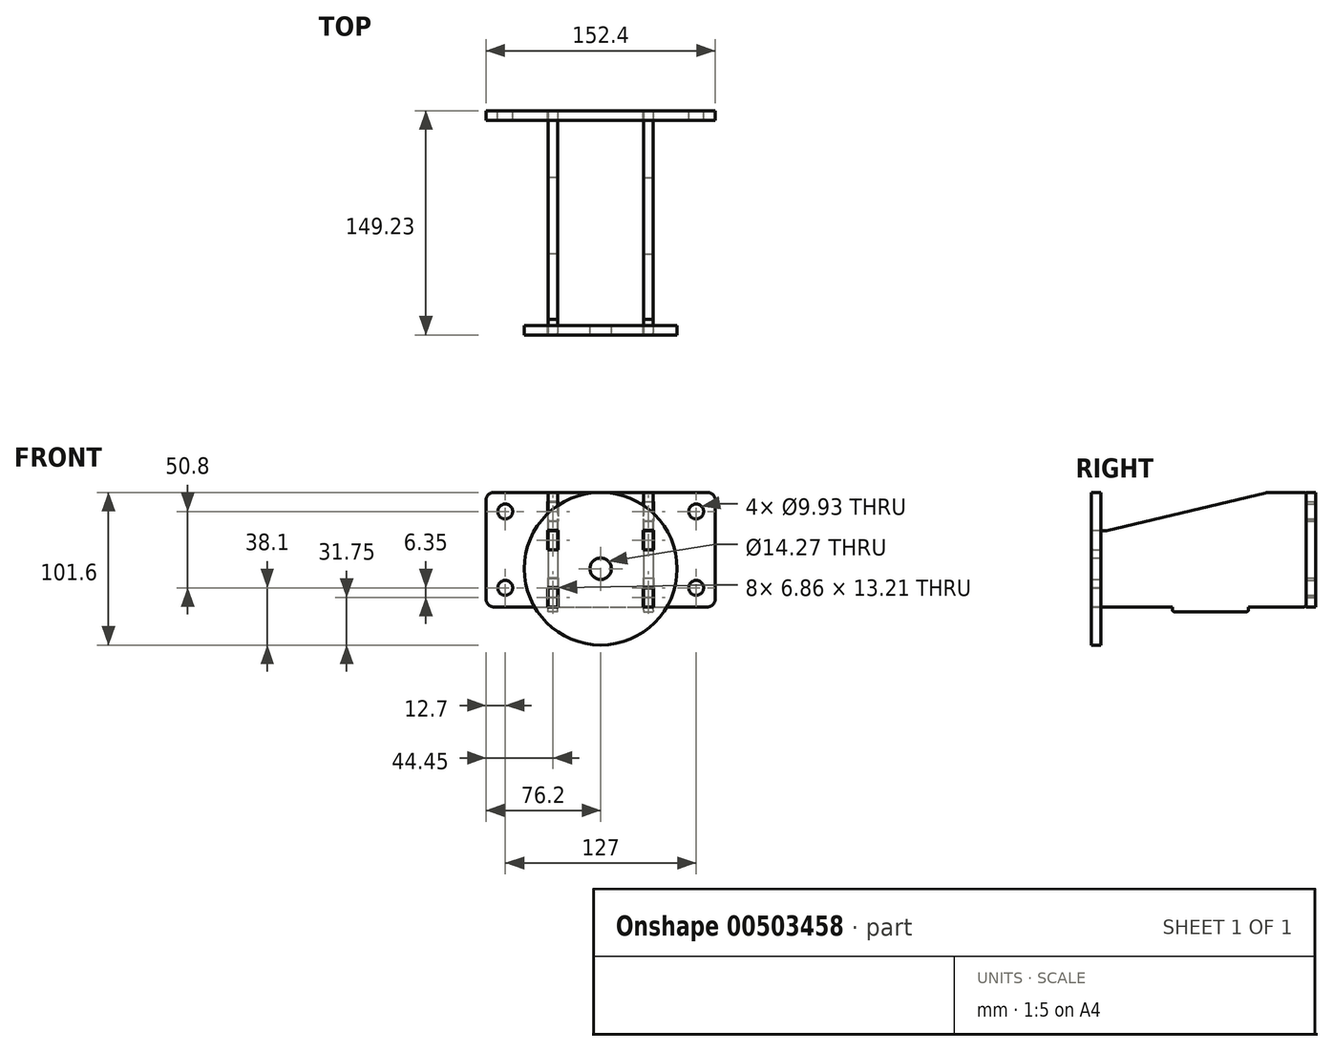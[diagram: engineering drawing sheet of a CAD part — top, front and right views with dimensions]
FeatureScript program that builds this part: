
annotation { "Feature Type Name" : "Feature", "Feature Type Description" : "" }
export const myFeature = defineFeature(function(context is Context, id is Id, definition is map)
    precondition{}
    {
        {
            var Q0;
            Q0=qCreatedBy(makeId("Front.planeOp"),FACE);
            var sketch = newSketch(context, id + "F0", { "sketchPlane" : qUnion([Q0])});
            skCircle(sketch, "E0", {"center": v(0, 0) * mm, "radius": 50.8 * mm});
            skCircle(sketch, "E1", {"center": v(0, 0) * mm, "radius": 7.14 * mm});
            skLineSegment(sketch, "E2.bottom", {"start": v(-28.58, 25.4) * mm, "end": v(-34.93, 25.4) * mm});
            skLineSegment(sketch, "E2.top", {"start": v(-28.57, -25.4) * mm, "end": v(-34.92, -25.4) * mm});
            skLineSegment(sketch, "E2.left", {"start": v(-28.58, 25.4) * mm, "end": v(-28.57, -25.4) * mm});
            skLineSegment(sketch, "E2.right", {"start": v(-34.93, 25.4) * mm, "end": v(-34.93, -25.4) * mm});
            skPoint(sketch, "E2.middle", {"position": v(-31.75, 0) * mm});
            skLineSegment(sketch, "E3.bottom", {"start": v(-35.18, 25.65) * mm, "end": v(-28.32, 25.65) * mm});
            skLineSegment(sketch, "E3.top", {"start": v(-35.18, 12.45) * mm, "end": v(-28.32, 12.45) * mm});
            skLineSegment(sketch, "E3.left", {"start": v(-35.18, 25.65) * mm, "end": v(-35.18, 12.45) * mm});
            skLineSegment(sketch, "E3.right", {"start": v(-28.32, 25.65) * mm, "end": v(-28.32, 12.45) * mm});
            skLineSegment(sketch, "E4.MirrorCS", {"start": v(-28.32, -25.65) * mm, "end": v(-28.32, -12.45) * mm});
            skLineSegment(sketch, "E5.MirrorCS", {"start": v(-35.18, -25.65) * mm, "end": v(-35.18, -12.45) * mm});
            skLineSegment(sketch, "E6.MirrorCS", {"start": v(-35.18, -25.65) * mm, "end": v(-28.32, -25.65) * mm});
            skLineSegment(sketch, "E7.MirrorCS", {"start": v(-35.18, -12.45) * mm, "end": v(-28.32, -12.45) * mm});
            skLineSegment(sketch, "E8.MirrorCS", {"start": v(28.58, 25.4) * mm, "end": v(28.57, -25.4) * mm});
            skLineSegment(sketch, "E9.MirrorCS", {"start": v(35.18, -25.65) * mm, "end": v(28.32, -25.65) * mm});
            skLineSegment(sketch, "E10.MirrorCS", {"start": v(35.18, -25.65) * mm, "end": v(35.18, -12.45) * mm});
            skLineSegment(sketch, "E11.MirrorCS", {"start": v(35.18, 12.45) * mm, "end": v(28.32, 12.45) * mm});
            skLineSegment(sketch, "E12.MirrorCS", {"start": v(28.58, 25.4) * mm, "end": v(34.93, 25.4) * mm});
            skLineSegment(sketch, "E13.MirrorCS", {"start": v(35.18, 25.65) * mm, "end": v(28.32, 25.65) * mm});
            skLineSegment(sketch, "E14.MirrorCS", {"start": v(35.18, 25.65) * mm, "end": v(35.18, 12.45) * mm});
            skLineSegment(sketch, "E15.MirrorCS", {"start": v(35.18, -12.45) * mm, "end": v(28.32, -12.45) * mm});
            skLineSegment(sketch, "E16.MirrorCS", {"start": v(28.32, 25.65) * mm, "end": v(28.32, 12.45) * mm});
            skLineSegment(sketch, "E17.MirrorCS", {"start": v(28.32, -25.65) * mm, "end": v(28.32, -12.45) * mm});
            skLineSegment(sketch, "E18.MirrorCS", {"start": v(28.57, -25.4) * mm, "end": v(34.92, -25.4) * mm});
            skPoint(sketch, "E19.MirrorP", {"position": v(31.75, 0) * mm});
            skLineSegment(sketch, "E20.MirrorCS", {"start": v(34.93, 25.4) * mm, "end": v(34.93, -25.4) * mm});
            skLineSegment(sketch, "E21", {"start": v(28.57, 12.7) * mm, "end": v(34.93, 12.7) * mm});
            skLineSegment(sketch, "E22", {"start": v(28.57, -12.7) * mm, "end": v(34.93, -12.7) * mm});
            skLineSegment(sketch, "E23", {"start": v(-34.92, -12.7) * mm, "end": v(-28.57, -12.7) * mm});
            skLineSegment(sketch, "E24", {"start": v(-34.93, 12.7) * mm, "end": v(-28.57, 12.7) * mm});
            skSolve(sketch);
        }
        {
            var Q0;
            Q0=makeQuery(id+"F0.imprint","IMPRINT",FACE,{"disambiguationData":[TD([[makeQuery(id+"F0.imprint","IMPRINT",EDGE,{"derivedFrom":sQuery(id+"F0.wireOp",EDGE,"E0")}),1.0]])]});
            var Q1;
            {var subQ0=sQuery(id+"F0.wireOp",EDGE,"E3.top");var subQ1=sQuery(id+"F0.wireOp",EDGE,"E2.left");var subQ2=makeQuery(id+"F0.imprint","INTERSECT",VERTEX,{"derivedFrom":[subQ1,subQ0]});Q1=makeQuery(id+"F0.imprint","IMPRINT",FACE,{"disambiguationData":[TD([[makeQuery(id+"F0.imprint","IMPRINT",EDGE,{"disambiguationData":[TD([[subQ2,-1.0]])],"derivedFrom":subQ1}),-1.0]])]});}
            var Q2;
            {var subQ0=sQuery(id+"F0.wireOp",EDGE,"E11.MirrorCS");var subQ1=sQuery(id+"F0.wireOp",EDGE,"E8.MirrorCS");var subQ2=makeQuery(id+"F0.imprint","INTERSECT",VERTEX,{"derivedFrom":[subQ1,subQ0]});Q2=makeQuery(id+"F0.imprint","IMPRINT",FACE,{"disambiguationData":[TD([[makeQuery(id+"F0.imprint","IMPRINT",EDGE,{"disambiguationData":[TD([[subQ2,-1.0]])],"derivedFrom":subQ1}),1.0]])]});}
            extrude(context, id + "F1", {"entities" : qUnion([Q0, Q1, Q2]), "depth" : 6.35 * mm, "offsetDistance" : 25.4 * mm});
        }
        {
            var Q0;
            {var subQ0=sQuery(id+"F0.wireOp",EDGE,"E12.MirrorCS");Q0=makeQuery(id+"F0.imprint","IMPRINT",FACE,{"disambiguationData":[TD([[makeQuery(id+"F0.imprint","IMPRINT",EDGE,{"derivedFrom":subQ0}),-1.0]])]});}
            var Q1;
            {var subQ0=sQuery(id+"F0.wireOp",EDGE,"E11.MirrorCS");var subQ1=sQuery(id+"F0.wireOp",EDGE,"E8.MirrorCS");var subQ2=makeQuery(id+"F0.imprint","INTERSECT",VERTEX,{"derivedFrom":[subQ1,subQ0]});Q1=makeQuery(id+"F0.imprint","IMPRINT",FACE,{"disambiguationData":[TD([[makeQuery(id+"F0.imprint","IMPRINT",EDGE,{"disambiguationData":[TD([[subQ2,-1.0]])],"derivedFrom":subQ1}),1.0]])]});}
            var Q2;
            {var subQ0=sQuery(id+"F0.wireOp",EDGE,"E18.MirrorCS");Q2=makeQuery(id+"F0.imprint","IMPRINT",FACE,{"disambiguationData":[TD([[makeQuery(id+"F0.imprint","IMPRINT",EDGE,{"derivedFrom":subQ0}),1.0]])]});}
            var Q3;
            {var subQ0=sQuery(id+"F0.wireOp",EDGE,"E21");Q3=makeQuery(id+"F0.imprint","IMPRINT",FACE,{"disambiguationData":[TD([[makeQuery(id+"F0.imprint","IMPRINT",EDGE,{"derivedFrom":subQ0}),-1.0]])]});}
            var Q4;
            {var subQ0=sQuery(id+"F0.wireOp",EDGE,"E22");Q4=makeQuery(id+"F0.imprint","IMPRINT",FACE,{"disambiguationData":[TD([[makeQuery(id+"F0.imprint","IMPRINT",EDGE,{"derivedFrom":subQ0}),1.0]])]});}
            var Q5;
            Q5=sQuery(id+"F0.wireOp",EDGE,"E2.right");
            var Q6;
            Q6=sQuery(id+"F0.wireOp",EDGE,"E2.bottom");
            var Q7;
            Q7=sQuery(id+"F0.wireOp",EDGE,"E2.left");
            var Q8;
            Q8=sQuery(id+"F0.wireOp",EDGE,"E2.top");
            var Q9;
            Q9=sQuery(id+"F0.wireOp",EDGE,"E12.MirrorCS");
            var Q10;
            Q10=sQuery(id+"F0.wireOp",EDGE,"E8.MirrorCS");
            var Q11;
            Q11=sQuery(id+"F0.wireOp",EDGE,"E20.MirrorCS");
            var Q12;
            Q12=sQuery(id+"F0.wireOp",EDGE,"E18.MirrorCS");
            extrude(context, id + "F2", {"entities" : qUnion([Q0, Q1, Q2, Q3, Q4]), "surfaceEntities" : qUnion([Q5, Q6, Q7, Q8, Q9, Q10, Q11, Q12]), "oppositeDirection" : true, "depth" : 136.53 * mm, "offsetDistance" : 25.4 * mm});
        }
        {
            var Q0;
            {var subQ0=sQuery(id+"F0.wireOp",EDGE,"E12.MirrorCS");Q0=makeQuery(id+"F0.imprint","IMPRINT",FACE,{"disambiguationData":[TD([[makeQuery(id+"F0.imprint","IMPRINT",EDGE,{"derivedFrom":subQ0}),-1.0]])]});}
            var Q1;
            {var subQ0=sQuery(id+"F0.wireOp",EDGE,"E18.MirrorCS");Q1=makeQuery(id+"F0.imprint","IMPRINT",FACE,{"disambiguationData":[TD([[makeQuery(id+"F0.imprint","IMPRINT",EDGE,{"derivedFrom":subQ0}),1.0]])]});}
            var Q2;
            Q2=sQuery(id+"F0.wireOp",EDGE,"E21");
            extrude(context, id + "F3", {"entities" : qUnion([Q0, Q1]), "operationType" : NewBodyOperationType.ADD, "surfaceOperationType" : NewSurfaceOperationType.ADD, "surfaceEntities" : qUnion([Q2]), "depth" : 6.1 * mm, "offsetDistance" : 25.4 * mm});
        }
        {
            var Q0;
            {var subQ0=sQuery(id+"F0.wireOp",EDGE,"E20.MirrorCS");Q0=makeQuery(id+"F3.boolean.opBoolean","MERGE",FACE,{"derivedFrom":[makeQuery(id+"F2.opExtrude","SWEPT_FACE",FACE,{"disambiguationData":[OSD([subQ0])]}),makeQuery(id+"F3.opExtrude","SWEPT_FACE",FACE,{"disambiguationData":[OSD([subQ0]),TDD([makeQuery(id+"F0.imprint","IMPRINT",EDGE,{"disambiguationData":[TD([[makeQuery(id+"F0.imprint","INTERSECT",VERTEX,{"derivedFrom":[sQuery(id+"F0.wireOp",EDGE,"E12.MirrorCS"),subQ0]}),-1.0]])],"derivedFrom":subQ0})])]}),makeQuery(id+"F3.opExtrude","SWEPT_FACE",FACE,{"disambiguationData":[OSD([subQ0]),TDD([makeQuery(id+"F0.imprint","IMPRINT",EDGE,{"disambiguationData":[TD([[makeQuery(id+"F0.imprint","INTERSECT",VERTEX,{"derivedFrom":[sQuery(id+"F0.wireOp",EDGE,"E18.MirrorCS"),subQ0]}),1.0]])],"derivedFrom":subQ0})])]})]});}
            var sketch = newSketch(context, id + "F4", { "sketchPlane" : qUnion([Q0])});
            skLineSegment(sketch, "E25", {"start": v(136.52, -25.4) * mm, "end": v(136.52, 50.8) * mm});
            skLineSegment(sketch, "E26", {"start": v(136.52, 50.8) * mm, "end": v(111.12, 50.8) * mm});
            skLineSegment(sketch, "E27", {"start": v(136.53, -25.4) * mm, "end": v(3.9, -25.4) * mm});
            skLineSegment(sketch, "E28", {"start": v(3.9, -25.4) * mm, "end": v(3.9, 25.4) * mm});
            skLineSegment(sketch, "E29", {"start": v(3.9, 25.4) * mm, "end": v(111.13, 50.8) * mm});
            skSolve(sketch);
        }
        {
            var Q0;
            {var subQ5=sQuery(id+"F4.wireOp",EDGE,"E26");Q0=makeQuery(id+"F4.imprint","IMPRINT",FACE,{"disambiguationData":[TD([[makeQuery(id+"F4.imprint","IMPRINT",EDGE,{"derivedFrom":subQ5}),1.0]])]});}
            extrude(context, id + "F5", {"entities" : qUnion([Q0]), "operationType" : NewBodyOperationType.ADD, "oppositeDirection" : true, "depth" : 6.35 * mm, "offsetDistance" : 25.4 * mm});
        }
        {
            var Q0;
            Q0=makeQuery(id+"F5.boolean.opBoolean","MERGE",FACE,{"derivedFrom":[makeQuery(id+"F2.opExtrude","CAP_FACE",FACE,{"disambiguationData":[OSD([sQuery(id+"F0.wireOp",EDGE,"E8.MirrorCS"),sQuery(id+"F0.wireOp",EDGE,"E12.MirrorCS"),sQuery(id+"F0.wireOp",EDGE,"E18.MirrorCS"),sQuery(id+"F0.wireOp",EDGE,"E20.MirrorCS")])],"isStart":false}),makeQuery(id+"F5.opExtrude","SWEPT_FACE",FACE,{"disambiguationData":[OSD([sQuery(id+"F4.wireOp",EDGE,"E25")])]})]});
            var sketch = newSketch(context, id + "F6", { "sketchPlane" : qUnion([Q0])});
            skLineSegment(sketch, "E30", {"start": v(-34.93, 44.45) * mm, "end": v(-28.58, 44.45) * mm});
            skLineSegment(sketch, "E31", {"start": v(-34.93, 31.75) * mm, "end": v(-28.58, 31.75) * mm});
            skLineSegment(sketch, "E32", {"start": v(-34.93, -19.05) * mm, "end": v(-28.58, -19.05) * mm});
            skLineSegment(sketch, "E33", {"start": v(-34.93, -6.35) * mm, "end": v(-28.58, -6.35) * mm});
            skSolve(sketch);
        }
        {
            var Q0;
            {var subQ0=sQuery(id+"F6.wireOp",EDGE,"E30");Q0=makeQuery(id+"F6.imprint","IMPRINT",FACE,{"disambiguationData":[TD([[makeQuery(id+"F6.imprint","IMPRINT",EDGE,{"derivedFrom":subQ0}),-1.0]])]});}
            var Q1;
            {var subQ0=sQuery(id+"F6.wireOp",EDGE,"E32");Q1=makeQuery(id+"F6.imprint","IMPRINT",FACE,{"disambiguationData":[TD([[makeQuery(id+"F6.imprint","IMPRINT",EDGE,{"derivedFrom":subQ0}),1.0]])]});}
            extrude(context, id + "F7", {"entities" : qUnion([Q0, Q1]), "operationType" : NewBodyOperationType.ADD, "depth" : 6.1 * mm, "offsetDistance" : 25.4 * mm});
        }
        {
            var Q0;
            Q0=makeQuery(id+"F3.opExtrude","CAP_EDGE",EDGE,{"disambiguationData":[OSD([sQuery(id+"F0.wireOp",EDGE,"E12.MirrorCS")])],"isStart":false});
            var Q1;
            Q1=makeQuery(id+"F3.opExtrude","CAP_EDGE",EDGE,{"disambiguationData":[OSD([sQuery(id+"F0.wireOp",EDGE,"E21")])],"isStart":false});
            var Q2;
            Q2=makeQuery(id+"F3.opExtrude","CAP_EDGE",EDGE,{"disambiguationData":[OSD([sQuery(id+"F0.wireOp",EDGE,"E22")])],"isStart":false});
            var Q3;
            Q3=makeQuery(id+"F3.opExtrude","CAP_EDGE",EDGE,{"disambiguationData":[OSD([sQuery(id+"F0.wireOp",EDGE,"E18.MirrorCS")])],"isStart":false});
            var Q4;
            Q4=makeQuery(id+"F7.opExtrude","CAP_EDGE",EDGE,{"disambiguationData":[OSD([sQuery(id+"F6.wireOp",EDGE,"E32")])],"isStart":false});
            var Q5;
            Q5=makeQuery(id+"F7.opExtrude","CAP_EDGE",EDGE,{"disambiguationData":[OSD([sQuery(id+"F6.wireOp",EDGE,"E33")])],"isStart":false});
            var Q6;
            Q6=makeQuery(id+"F7.opExtrude","CAP_EDGE",EDGE,{"disambiguationData":[OSD([sQuery(id+"F6.wireOp",EDGE,"E31")])],"isStart":false});
            var Q7;
            Q7=makeQuery(id+"F7.opExtrude","CAP_EDGE",EDGE,{"disambiguationData":[OSD([sQuery(id+"F6.wireOp",EDGE,"E30")])],"isStart":false});
            var Q8;
            Q8=makeQuery(id+"F2.opExtrude","CAP_EDGE",EDGE,{"disambiguationData":[OSD([sQuery(id+"F0.wireOp",EDGE,"E18.MirrorCS")])],"isStart":false});
            var Q9;
            Q9=makeQuery(id+"F5.opExtrude","SWEPT_EDGE",EDGE,{"disambiguationData":[OSD([sQuery(id+"F4.wireOp",EDGE,"E25"),sQuery(id+"F4.wireOp",EDGE,"E26")])]});
            fillet(context, id + "F8", {"entities" : qUnion([Q0, Q1, Q2, Q3, Q4, Q5, Q6, Q7, Q8, Q9]), "radius" : 1.27 * mm, "tangentPropagation" : true, "allowEdgeOverflow" : false});
        }
        {
            var Q0;
            Q0=makeQuery(id+"F5.opExtrude","SWEPT_EDGE",EDGE,{"disambiguationData":[OSD([sQuery(id+"F0.wireOp",EDGE,"E12.MirrorCS"),sQuery(id+"F0.wireOp",EDGE,"E20.MirrorCS"),sQuery(id+"F4.wireOp",EDGE,"E28"),sQuery(id+"F4.wireOp",EDGE,"E29")])]});
            var Q1;
            Q1=makeQuery(id+"F5.opExtrude","SWEPT_EDGE",EDGE,{"disambiguationData":[OSD([sQuery(id+"F4.wireOp",EDGE,"E26"),sQuery(id+"F4.wireOp",EDGE,"E29")])]});
            fillet(context, id + "F9", {"entities" : qUnion([Q0, Q1]), "radius" : 12.7 * mm, "allowEdgeOverflow" : false});
        }
        {
            var Q0;
            Q0=makeQuery(id+"F7.opExtrude","CAP_FACE",FACE,{"disambiguationData":[OSD([sQuery(id+"F0.wireOp",EDGE,"E8.MirrorCS"),sQuery(id+"F0.wireOp",EDGE,"E20.MirrorCS"),sQuery(id+"F4.wireOp",EDGE,"E25"),sQuery(id+"F6.wireOp",EDGE,"E30"),sQuery(id+"F6.wireOp",EDGE,"E31")])],"isStart":false});
            var sketch = newSketch(context, id + "F10", { "sketchPlane" : qUnion([Q0])});
            skLineSegment(sketch, "E34", {"start": v(-95.05, -25.4) * mm, "end": v(104.43, -25.4) * mm, "construction": true});
            skLineSegment(sketch, "E35", {"start": v(-97.99, 50.8) * mm, "end": v(99.94, 50.8) * mm, "construction": true});
            skLineSegment(sketch, "E36", {"start": v(-76.2, 66.04) * mm, "end": v(-76.2, -54.32) * mm, "construction": true});
            skLineSegment(sketch, "E37", {"start": v(99.84, 72.1) * mm, "end": v(99.84, -54.32) * mm, "construction": true});
            skLineSegment(sketch, "E38.bottom", {"start": v(-76.2, 50.8) * mm, "end": v(0, 50.8) * mm});
            skLineSegment(sketch, "E38.top", {"start": v(-76.2, -25.4) * mm, "end": v(0, -25.4) * mm});
            skLineSegment(sketch, "E38.left", {"start": v(-76.2, 50.8) * mm, "end": v(-76.2, -25.4) * mm});
            skLineSegment(sketch, "E38.right", {"start": v(0, 50.8) * mm, "end": v(0, -25.4) * mm});
            skLineSegment(sketch, "E39.MirrorCS", {"start": v(76.2, -25.4) * mm, "end": v(0, -25.4) * mm});
            skLineSegment(sketch, "E40.MirrorCS", {"start": v(76.2, 50.8) * mm, "end": v(0, 50.8) * mm});
            skLineSegment(sketch, "E41.MirrorCS", {"start": v(76.2, 50.8) * mm, "end": v(76.2, -25.4) * mm});
            skCircle(sketch, "E42", {"center": v(-63.5, 38.1) * mm, "radius": 4.97 * mm});
            skCircle(sketch, "E43", {"center": v(-63.5, -12.7) * mm, "radius": 4.97 * mm});
            skCircle(sketch, "E44.MirrorC", {"center": v(63.5, 38.1) * mm, "radius": 4.97 * mm});
            skCircle(sketch, "E45.MirrorC", {"center": v(63.5, -12.7) * mm, "radius": 4.97 * mm});
            skLineSegment(sketch, "E46.bottom", {"start": v(-28.32, 44.7) * mm, "end": v(-35.18, 44.7) * mm});
            skLineSegment(sketch, "E46.top", {"start": v(-28.32, 31.5) * mm, "end": v(-35.18, 31.5) * mm});
            skLineSegment(sketch, "E46.left", {"start": v(-28.32, 44.7) * mm, "end": v(-28.32, 31.5) * mm});
            skLineSegment(sketch, "E46.right", {"start": v(-35.18, 44.7) * mm, "end": v(-35.18, 31.5) * mm});
            skLineSegment(sketch, "E47.0", {"start": v(-34.93, -6.35) * mm, "end": v(-34.93, -19.05) * mm});
            skLineSegment(sketch, "E48.0", {"start": v(-34.93, -6.35) * mm, "end": v(-28.58, -6.35) * mm});
            skLineSegment(sketch, "E49.0", {"start": v(-34.93, -19.05) * mm, "end": v(-28.58, -19.05) * mm});
            skLineSegment(sketch, "E50.0", {"start": v(-28.58, -6.35) * mm, "end": v(-28.58, -19.05) * mm});
            skLineSegment(sketch, "E51.bottom", {"start": v(-28.32, -6.1) * mm, "end": v(-35.18, -6.1) * mm});
            skLineSegment(sketch, "E51.top", {"start": v(-28.32, -19.3) * mm, "end": v(-35.18, -19.3) * mm});
            skLineSegment(sketch, "E51.left", {"start": v(-28.32, -6.1) * mm, "end": v(-28.32, -19.3) * mm});
            skLineSegment(sketch, "E51.right", {"start": v(-35.18, -6.1) * mm, "end": v(-35.18, -19.3) * mm});
            skLineSegment(sketch, "E52.MirrorCS", {"start": v(28.32, -6.1) * mm, "end": v(35.18, -6.1) * mm});
            skLineSegment(sketch, "E53.MirrorCS", {"start": v(34.93, -6.35) * mm, "end": v(28.58, -6.35) * mm});
            skLineSegment(sketch, "E54.MirrorCS", {"start": v(28.32, -19.3) * mm, "end": v(35.18, -19.3) * mm});
            skLineSegment(sketch, "E55.MirrorCS", {"start": v(28.32, 44.7) * mm, "end": v(35.18, 44.7) * mm});
            skLineSegment(sketch, "E56.MirrorCS", {"start": v(28.32, 31.5) * mm, "end": v(35.18, 31.5) * mm});
            skLineSegment(sketch, "E57.MirrorCS", {"start": v(34.93, -19.05) * mm, "end": v(28.58, -19.05) * mm});
            skLineSegment(sketch, "E58.MirrorCS", {"start": v(35.18, -6.1) * mm, "end": v(35.18, -19.3) * mm});
            skLineSegment(sketch, "E59.MirrorCS", {"start": v(28.58, -6.35) * mm, "end": v(28.58, -19.05) * mm});
            skLineSegment(sketch, "E60.MirrorCS", {"start": v(28.32, 44.7) * mm, "end": v(28.32, 31.5) * mm});
            skLineSegment(sketch, "E61.MirrorCS", {"start": v(35.18, 44.7) * mm, "end": v(35.18, 31.5) * mm});
            skLineSegment(sketch, "E62.MirrorCS", {"start": v(28.32, -6.1) * mm, "end": v(28.32, -19.3) * mm});
            skLineSegment(sketch, "E63.MirrorCS", {"start": v(34.93, -6.35) * mm, "end": v(34.93, -19.05) * mm});
            skSolve(sketch);
        }
        {
            var Q0;
            Q0=makeQuery(id+"F10.imprint","IMPRINT",FACE,{"disambiguationData":[TD([[makeQuery(id+"F10.imprint","IMPRINT",EDGE,{"derivedFrom":sQuery(id+"F10.wireOp",EDGE,"kh7ab5N3-OJCW-Qjtw-u9Ue-FteD8OsjeyxH.bottom")}),1.0]])]});
            var Q1;
            Q1=makeQuery(id+"F10.imprint","IMPRINT",FACE,{"disambiguationData":[TD([[makeQuery(id+"F10.imprint","IMPRINT",EDGE,{"derivedFrom":sQuery(id+"F10.wireOp",EDGE,"E38.right")}),1.0]])]});
            var Q2;
            Q2=makeQuery(id+"F10.imprint","IMPRINT",FACE,{"disambiguationData":[TD([[makeQuery(id+"F10.imprint","IMPRINT",EDGE,{"derivedFrom":sQuery(id+"F10.wireOp",EDGE,"E38.bottom")}),-1.0]])]});
            extrude(context, id + "F11", {"entities" : qUnion([Q0, Q1, Q2]), "oppositeDirection" : true, "depth" : 6.35 * mm, "offsetDistance" : 25.4 * mm});
        }
        {
            var Q0;
            Q0=makeQuery(id+"F11.opExtrude","SWEPT_EDGE",EDGE,{"disambiguationData":[OSD([sQuery(id+"F10.wireOp",EDGE,"E38.bottom"),sQuery(id+"F10.wireOp",EDGE,"E38.left")])]});
            var Q1;
            Q1=makeQuery(id+"F11.opExtrude","SWEPT_EDGE",EDGE,{"disambiguationData":[OSD([sQuery(id+"F10.wireOp",EDGE,"E38.top"),sQuery(id+"F10.wireOp",EDGE,"E38.left")])]});
            var Q2;
            Q2=makeQuery(id+"F11.opExtrude","SWEPT_EDGE",EDGE,{"disambiguationData":[OSD([sQuery(id+"F10.wireOp",EDGE,"E39.MirrorCS"),sQuery(id+"F10.wireOp",EDGE,"E41.MirrorCS")])]});
            var Q3;
            Q3=makeQuery(id+"F11.opExtrude","SWEPT_EDGE",EDGE,{"disambiguationData":[OSD([sQuery(id+"F10.wireOp",EDGE,"E40.MirrorCS"),sQuery(id+"F10.wireOp",EDGE,"E41.MirrorCS")])]});
            fillet(context, id + "F12", {"entities" : qUnion([Q0, Q1, Q2, Q3]), "radius" : 5.08 * mm, "tangentPropagation" : true, "allowEdgeOverflow" : false});
        }
        {
            var Q0;
            Q0=makeQuery(id+"F2.opExtrude","SWEPT_BODY",BODY,{"disambiguationData":[OSD([sQuery(id+"F0.wireOp",EDGE,"E8.MirrorCS"),sQuery(id+"F0.wireOp",EDGE,"E12.MirrorCS"),sQuery(id+"F0.wireOp",EDGE,"E18.MirrorCS"),sQuery(id+"F0.wireOp",EDGE,"E20.MirrorCS")])]});
            var Q1;
            Q1=qCreatedBy(makeId("Right.planeOp"),FACE);
            mirror(context, id + "F13", {"entities" : qUnion([Q0]), "mirrorPlane" : qUnion([Q1])});
        }
        {
            var Q0;
            Q0=makeQuery(id+"F11.opExtrude","SWEPT_BODY",BODY,{"disambiguationData":[OSD([sQuery(id+"F10.wireOp",EDGE,"kh7ab5N3-OJCW-Qjtw-u9Ue-FteD8OsjeyxH.bottom"),sQuery(id+"F10.wireOp",EDGE,"kh7ab5N3-OJCW-Qjtw-u9Ue-FteD8OsjeyxH.top"),sQuery(id+"F10.wireOp",EDGE,"kh7ab5N3-OJCW-Qjtw-u9Ue-FteD8OsjeyxH.left"),sQuery(id+"F10.wireOp",EDGE,"kh7ab5N3-OJCW-Qjtw-u9Ue-FteD8OsjeyxH.right"),sQuery(id+"F10.wireOp",EDGE,"07f8240c-9034-471a-aabd-449adbaa0d79.bottom"),sQuery(id+"F10.wireOp",EDGE,"07f8240c-9034-471a-aabd-449adbaa0d79.top"),sQuery(id+"F10.wireOp",EDGE,"07f8240c-9034-471a-aabd-449adbaa0d79.left"),sQuery(id+"F10.wireOp",EDGE,"07f8240c-9034-471a-aabd-449adbaa0d79.right"),sQuery(id+"F10.wireOp",EDGE,"E38.bottom"),sQuery(id+"F10.wireOp",EDGE,"E38.top"),sQuery(id+"F10.wireOp",EDGE,"E38.left"),sQuery(id+"F10.wireOp",EDGE,"c66714a7-deac-4855-aefa-6b8c5e85cdf00.MirrorCS"),sQuery(id+"F10.wireOp",EDGE,"c66714a7-deac-4855-aefa-6b8c5e85cdf01.MirrorCS"),sQuery(id+"F10.wireOp",EDGE,"E39.MirrorCS"),sQuery(id+"F10.wireOp",EDGE,"c66714a7-deac-4855-aefa-6b8c5e85cdf03.MirrorCS"),sQuery(id+"F10.wireOp",EDGE,"c66714a7-deac-4855-aefa-6b8c5e85cdf04.MirrorCS"),sQuery(id+"F10.wireOp",EDGE,"E40.MirrorCS"),sQuery(id+"F10.wireOp",EDGE,"E41.MirrorCS"),sQuery(id+"F10.wireOp",EDGE,"c66714a7-deac-4855-aefa-6b8c5e85cdf07.MirrorCS"),sQuery(id+"F10.wireOp",EDGE,"c66714a7-deac-4855-aefa-6b8c5e85cdf08.MirrorCS"),sQuery(id+"F10.wireOp",EDGE,"c66714a7-deac-4855-aefa-6b8c5e85cdf09.MirrorCS"),sQuery(id+"F10.wireOp",EDGE,"c66714a7-deac-4855-aefa-6b8c5e85cdf010.MirrorCS"),sQuery(id+"F10.wireOp",EDGE,"E42"),sQuery(id+"F10.wireOp",EDGE,"E43"),sQuery(id+"F10.wireOp",EDGE,"E44.MirrorC"),sQuery(id+"F10.wireOp",EDGE,"E45.MirrorC")])]});
            transform(context, id + "F14", {"entities" : qUnion([Q0]), "transformType" : TransformType.TRANSLATION_3D, "dx" : 0 * mm, "dy" : 0.25 * mm, "dz" : 0 * mm, "makeCopy" : false});
        }
        {
            var Q0;
            {var subQ0=sQuery(id+"F4.wireOp",EDGE,"E25");var subQ1=sQuery(id+"F0.wireOp",EDGE,"E20.MirrorCS");var subQ2=makeQuery(id+"F5.boolean.opBoolean","MERGE",EDGE,{"derivedFrom":[makeQuery(id+"F2.opExtrude","CAP_EDGE",EDGE,{"disambiguationData":[OSD([subQ1])],"isStart":false}),makeQuery(id+"F5.opExtrude","CAP_EDGE",EDGE,{"disambiguationData":[OSD([subQ0])],"isStart":true})]});var subQ3=sQuery(id+"F0.wireOp",EDGE,"E12.MirrorCS");Q0=makeQuery(id+"F7.boolean.opBoolean","MERGE",FACE,{"derivedFrom":[makeQuery(id+"F5.boolean.opBoolean","MERGE",FACE,{"derivedFrom":[makeQuery(id+"F3.boolean.opBoolean","MERGE",FACE,{"derivedFrom":[makeQuery(id+"F2.opExtrude","SWEPT_FACE",FACE,{"disambiguationData":[OSD([subQ1])]}),makeQuery(id+"F3.opExtrude","SWEPT_FACE",FACE,{"disambiguationData":[OSD([subQ1]),TDD([makeQuery(id+"F0.imprint","IMPRINT",EDGE,{"disambiguationData":[TD([[makeQuery(id+"F0.imprint","INTERSECT",VERTEX,{"derivedFrom":[subQ3,subQ1]}),-1.0]])],"derivedFrom":subQ1})])]}),makeQuery(id+"F3.opExtrude","SWEPT_FACE",FACE,{"disambiguationData":[OSD([subQ1]),TDD([makeQuery(id+"F0.imprint","IMPRINT",EDGE,{"disambiguationData":[TD([[makeQuery(id+"F0.imprint","INTERSECT",VERTEX,{"derivedFrom":[sQuery(id+"F0.wireOp",EDGE,"E18.MirrorCS"),subQ1]}),1.0]])],"derivedFrom":subQ1})])]})]}),makeQuery(id+"F5.opExtrude","CAP_FACE",FACE,{"disambiguationData":[OSD([subQ3,subQ1,subQ0,sQuery(id+"F4.wireOp",EDGE,"E26"),sQuery(id+"F4.wireOp",EDGE,"E29")])],"isStart":true})]}),makeQuery(id+"F7.opExtrude","SWEPT_FACE",FACE,{"disambiguationData":[OSD([subQ1,subQ0]),TDD([makeQuery(id+"F6.imprint","IMPRINT",EDGE,{"disambiguationData":[TD([[makeQuery(id+"F6.imprint","INTERSECT",VERTEX,{"derivedFrom":[subQ2,sQuery(id+"F6.wireOp",EDGE,"E30")]}),-1.0]])],"derivedFrom":subQ2})])]}),makeQuery(id+"F7.opExtrude","SWEPT_FACE",FACE,{"disambiguationData":[OSD([subQ1,subQ0]),TDD([makeQuery(id+"F6.imprint","IMPRINT",EDGE,{"disambiguationData":[TD([[makeQuery(id+"F6.imprint","INTERSECT",VERTEX,{"derivedFrom":[subQ2,sQuery(id+"F6.wireOp",EDGE,"E32")]}),1.0]])],"derivedFrom":subQ2})])]})]});}
            var sketch = newSketch(context, id + "F15", { "sketchPlane" : qUnion([Q0])});
            skLineSegment(sketch, "E64.top", {"start": v(98.43, -25.4) * mm, "end": v(43.19, -25.4) * mm});
            skLineSegment(sketch, "E65", {"start": v(43.19, -25.4) * mm, "end": v(98.43, -25.4) * mm});
            skLineSegment(sketch, "E66", {"start": v(47.63, -28.58) * mm, "end": v(47.63, -25.4) * mm});
            skLineSegment(sketch, "E67", {"start": v(43.19, -25.4) * mm, "end": v(47.63, -25.4) * mm});
            skLineSegment(sketch, "E68", {"start": v(47.63, -25.4) * mm, "end": v(98.43, -25.4) * mm});
            skLineSegment(sketch, "E69", {"start": v(47.63, -28.58) * mm, "end": v(98.43, -28.58) * mm});
            skLineSegment(sketch, "E70", {"start": v(98.43, -28.58) * mm, "end": v(98.43, -25.4) * mm});
            skSolve(sketch);
        }
        {
            var Q0;
            Q0=makeQuery(id+"F15.imprint","IMPRINT",FACE,{"disambiguationData":[TD([[makeQuery(id+"F15.imprint","IMPRINT",EDGE,{"derivedFrom":sQuery(id+"F15.wireOp",EDGE,"E66")}),-1.0]])]});
            extrude(context, id + "F16", {"entities" : qUnion([Q0]), "operationType" : NewBodyOperationType.ADD, "oppositeDirection" : true, "depth" : 6.35 * mm, "offsetDistance" : 25.4 * mm});
        }
        {
            var Q0;
            Q0=makeQuery(id+"F15.imprint","IMPRINT",FACE,{"disambiguationData":[TD([[makeQuery(id+"F15.imprint","IMPRINT",EDGE,{"derivedFrom":sQuery(id+"F15.wireOp",EDGE,"E66")}),-1.0]])]});
            extrude(context, id + "F17", {"entities" : qUnion([Q0]), "operationType" : NewBodyOperationType.ADD, "oppositeDirection" : true, "depth" : 6.35 * mm, "offsetDistance" : 25.4 * mm});
        }
        {
            var Q0;
            Q0=makeQuery(id+"F16.opExtrude","SWEPT_EDGE",EDGE,{"disambiguationData":[OSD([sQuery(id+"F15.wireOp",EDGE,"E66"),sQuery(id+"F15.wireOp",EDGE,"E69")])]});
            var Q1;
            Q1=makeQuery(id+"F16.opExtrude","SWEPT_EDGE",EDGE,{"disambiguationData":[OSD([sQuery(id+"F15.wireOp",EDGE,"E69"),sQuery(id+"F15.wireOp",EDGE,"E70")])]});
            var Q2;
            Q2=makeQuery(id+"F16.opExtrude","SWEPT_EDGE",EDGE,{"disambiguationData":[OSD([sQuery(id+"F0.wireOp",EDGE,"E18.MirrorCS"),sQuery(id+"F0.wireOp",EDGE,"E20.MirrorCS"),sQuery(id+"F15.wireOp",EDGE,"E68"),sQuery(id+"F15.wireOp",EDGE,"E70")])]});
            var Q3;
            Q3=makeQuery(id+"F16.opExtrude","SWEPT_EDGE",EDGE,{"disambiguationData":[OSD([sQuery(id+"F15.wireOp",EDGE,"E66"),sQuery(id+"F15.wireOp",EDGE,"E67"),sQuery(id+"F15.wireOp",EDGE,"E68")])]});
            fillet(context, id + "F18", {"entities" : qUnion([Q0, Q1, Q2, Q3]), "radius" : 1.27 * mm, "tangentPropagation" : true, "allowEdgeOverflow" : false});
        }
        {
            var Q0;
            Q0=makeQuery(id+"F2.opExtrude","SWEPT_BODY",BODY,{"disambiguationData":[OSD([sQuery(id+"F0.wireOp",EDGE,"E8.MirrorCS"),sQuery(id+"F0.wireOp",EDGE,"E12.MirrorCS"),sQuery(id+"F0.wireOp",EDGE,"E18.MirrorCS"),sQuery(id+"F0.wireOp",EDGE,"E20.MirrorCS")])]});
            var Q1;
            Q1=qCreatedBy(makeId("Right.planeOp"),FACE);
            mirror(context, id + "F19", {"entities" : qUnion([Q0]), "mirrorPlane" : qUnion([Q1])});
        }
        {
            var Q0;
            Q0=makeQuery(id+"F19.opPattern","COPY",BODY,{"derivedFrom":makeQuery(id+"F2.opExtrude","SWEPT_BODY",BODY,{"disambiguationData":[OSD([sQuery(id+"F0.wireOp",EDGE,"E8.MirrorCS"),sQuery(id+"F0.wireOp",EDGE,"E12.MirrorCS"),sQuery(id+"F0.wireOp",EDGE,"E18.MirrorCS"),sQuery(id+"F0.wireOp",EDGE,"E20.MirrorCS")])]}),"instanceName":"1"});
            deleteBodies(context, id + "F20", {"entities" : qUnion([Q0])});
        }
        {
            var Q0;
            Q0=makeQuery(id+"F13.opPattern","COPY",BODY,{"derivedFrom":makeQuery(id+"F2.opExtrude","SWEPT_BODY",BODY,{"disambiguationData":[OSD([sQuery(id+"F0.wireOp",EDGE,"E8.MirrorCS"),sQuery(id+"F0.wireOp",EDGE,"E12.MirrorCS"),sQuery(id+"F0.wireOp",EDGE,"E18.MirrorCS"),sQuery(id+"F0.wireOp",EDGE,"E20.MirrorCS")])]}),"instanceName":"1"});
            deleteBodies(context, id + "F21", {"entities" : qUnion([Q0])});
        }
        {
            var Q0;
            Q0=makeQuery(id+"F2.opExtrude","SWEPT_BODY",BODY,{"disambiguationData":[OSD([sQuery(id+"F0.wireOp",EDGE,"E8.MirrorCS"),sQuery(id+"F0.wireOp",EDGE,"E12.MirrorCS"),sQuery(id+"F0.wireOp",EDGE,"E18.MirrorCS"),sQuery(id+"F0.wireOp",EDGE,"E20.MirrorCS")])]});
            var Q1;
            Q1=qCreatedBy(makeId("Right.planeOp"),FACE);
            mirror(context, id + "F22", {"entities" : qUnion([Q0]), "mirrorPlane" : qUnion([Q1])});
        }
    });
